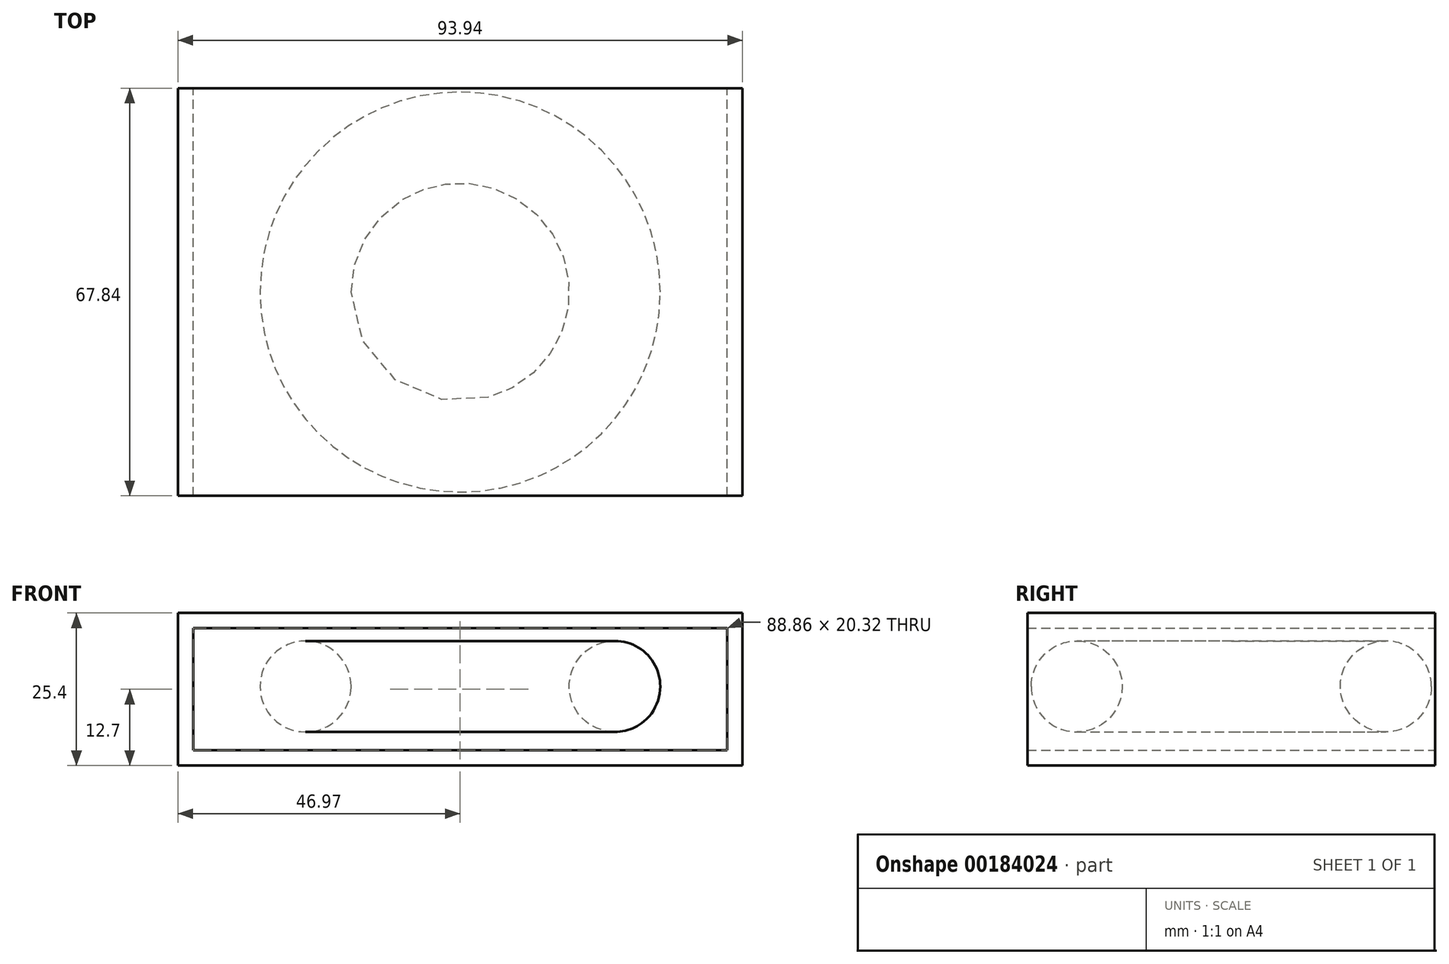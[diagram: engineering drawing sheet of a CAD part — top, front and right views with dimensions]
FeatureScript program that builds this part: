
annotation { "Feature Type Name" : "Feature", "Feature Type Description" : "" }
export const myFeature = defineFeature(function(context is Context, id is Id, definition is map)
    precondition{}
    {
        {
            var Q0;
            Q0=qCreatedBy(makeId("Top.planeOp"),FACE);
            var sketch = newSketch(context, id + "F0", { "sketchPlane" : qUnion([Q0])});
            skLineSegment(sketch, "E0.bottom", {"start": v(46.97, -33.92) * mm, "end": v(-46.97, -33.92) * mm});
            skLineSegment(sketch, "E0.top", {"start": v(46.97, 33.92) * mm, "end": v(-46.97, 33.92) * mm});
            skLineSegment(sketch, "E0.left", {"start": v(46.97, -33.92) * mm, "end": v(46.97, 33.92) * mm});
            skLineSegment(sketch, "E0.right", {"start": v(-46.97, -33.92) * mm, "end": v(-46.97, 33.92) * mm});
            skPoint(sketch, "E0.middle", {"position": v(0, 0) * mm});
            skSolve(sketch);
        }
        {
            var Q0;
            Q0=makeQuery(id+"F0.imprint","IMPRINT",FACE,{"disambiguationData":[TD([[makeQuery(id+"F0.imprint","IMPRINT",EDGE,{"derivedFrom":sQuery(id+"F0.wireOp",EDGE,"E0.bottom")}),-1.0]])]});
            extrude(context, id + "F1", {"entities" : qUnion([Q0]), "depth" : 25.4 * mm});
        }
        {
            var Q0;
            Q0=makeQuery(id+"F1.opExtrude","SWEPT_FACE",FACE,{"disambiguationData":[OSD([sQuery(id+"F0.wireOp",EDGE,"E0.bottom")])]});
            var Q1;
            Q1=makeQuery(id+"F1.opExtrude","SWEPT_FACE",FACE,{"disambiguationData":[OSD([sQuery(id+"F0.wireOp",EDGE,"E0.top")])]});
            shell(context, id + "F2", {"entities" : qUnion([Q0, Q1]), "thickness" : 2.54 * mm});
        }
        {
            var Q0;
            Q0=qCreatedBy(makeId("Front.planeOp"),FACE);
            var sketch = newSketch(context, id + "F3", { "sketchPlane" : qUnion([Q0])});
            skCircle(sketch, "E1", {"center": v(25.72, 13.18) * mm, "radius": 7.57 * mm});
            skLineSegment(sketch, "E2", {"start": v(0, 0) * mm, "end": v(0, 24.6) * mm});
            skSolve(sketch);
        }
        {
            var Q0;
            Q0=makeQuery(id+"F3.imprint","IMPRINT",FACE,{"disambiguationData":[TD([[makeQuery(id+"F3.imprint","IMPRINT",EDGE,{"derivedFrom":sQuery(id+"F3.wireOp",EDGE,"E1")}),1.0]])]});
            var Q1;
            Q1=sQuery(id+"F3.wireOp",EDGE,"E2");
            revolve(context, id + "F4", {"entities" : qUnion([Q0]), "axis" : qUnion([Q1]), "revolveType" : RevolveType.FULL});
        }
    });
